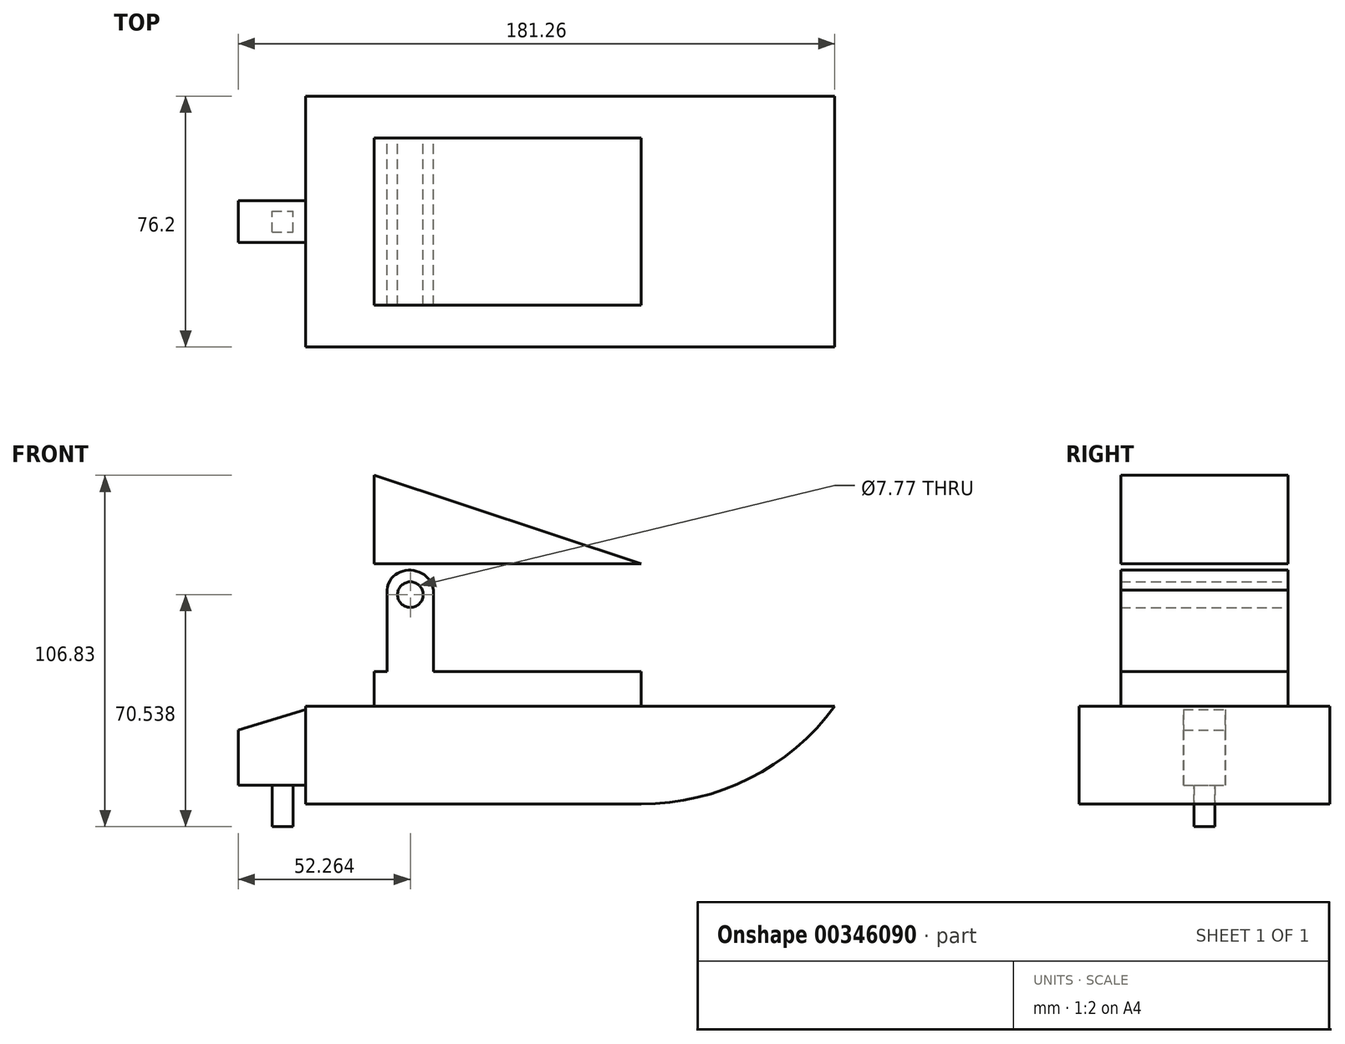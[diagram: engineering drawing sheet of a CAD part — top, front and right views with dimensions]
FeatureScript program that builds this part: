
annotation { "Feature Type Name" : "Feature", "Feature Type Description" : "" }
export const myFeature = defineFeature(function(context is Context, id is Id, definition is map)
    precondition{}
    {
        {
            var Q0;
            Q0=qCreatedBy(makeId("Front.planeOp"),FACE);
            var sketch = newSketch(context, id + "F0", { "sketchPlane" : qUnion([Q0])});
            skLineSegment(sketch, "E0", {"start": v(-51.12, -22.56) * mm, "end": v(50.84, -22.56) * mm});
            skArc(sketch, "E1", {"start": v(50.84, -22.56) * mm, "mid": v(83.8, -14.71) * mm, "end": v(109.67, 7.14) * mm});
            skLineSegment(sketch, "E2", {"start": v(-51.12, -22.56) * mm, "end": v(-51.12, 7.14) * mm});
            skLineSegment(sketch, "E3", {"start": v(-51.12, 7.14) * mm, "end": v(109.67, 7.14) * mm});
            skLineSegment(sketch, "E4", {"start": v(-30.27, 7.14) * mm, "end": v(-30.27, 17.7) * mm});
            skLineSegment(sketch, "E5", {"start": v(-30.27, 17.7) * mm, "end": v(-51.12, 17.7) * mm});
            skLineSegment(sketch, "E6", {"start": v(-51.12, 17.7) * mm, "end": v(-51.12, 7.14) * mm});
            skLineSegment(sketch, "E7", {"start": v(-30.27, 17.7) * mm, "end": v(109.67, 17.7) * mm});
            skLineSegment(sketch, "E8", {"start": v(109.67, 17.7) * mm, "end": v(109.67, 7.14) * mm});
            skLineSegment(sketch, "E9", {"start": v(-5.42, 17.7) * mm, "end": v(-5.42, 7.14) * mm});
            skLineSegment(sketch, "E10", {"start": v(-5.42, 7.14) * mm, "end": v(21.13, 7.14) * mm});
            skLineSegment(sketch, "E11", {"start": v(21.13, 7.14) * mm, "end": v(21.13, 17.7) * mm});
            skLineSegment(sketch, "E12", {"start": v(21.13, 17.7) * mm, "end": v(45.7, 17.7) * mm});
            skLineSegment(sketch, "E13", {"start": v(45.7, 17.7) * mm, "end": v(45.7, 7.14) * mm});
            skLineSegment(sketch, "E14", {"start": v(45.7, 7.14) * mm, "end": v(71.97, 7.14) * mm});
            skLineSegment(sketch, "E15", {"start": v(71.97, 7.14) * mm, "end": v(71.97, 17.7) * mm});
            skLineSegment(sketch, "E16", {"start": v(71.97, 17.7) * mm, "end": v(93.1, 17.7) * mm});
            skLineSegment(sketch, "E17", {"start": v(93.1, 17.7) * mm, "end": v(93.1, 7.14) * mm});
            skLineSegment(sketch, "E18.bottom", {"start": v(-30.27, 7.14) * mm, "end": v(50.84, 7.14) * mm});
            skLineSegment(sketch, "E18.left", {"start": v(-30.27, 7.14) * mm, "end": v(-30.27, 50.55) * mm});
            skLineSegment(sketch, "E18.right", {"start": v(50.84, 7.14) * mm, "end": v(50.84, 50.55) * mm});
            skLineSegment(sketch, "E19", {"start": v(-30.27, 50.55) * mm, "end": v(-30.27, 77.4) * mm});
            skLineSegment(sketch, "E20", {"start": v(-30.27, 77.4) * mm, "end": v(50.84, 50.55) * mm});
            skLineSegment(sketch, "E21", {"start": v(50.84, 50.55) * mm, "end": v(-30.27, 50.55) * mm});
            skCircle(sketch, "E22", {"center": v(-19.33, 41.1) * mm, "radius": 3.88 * mm});
            skLineSegment(sketch, "E23", {"start": v(-26.4, 7.14) * mm, "end": v(-26.4, 42.53) * mm});
            skFitSpline(sketch, "E24", {"points": [v(-26.4, 42.53) * mm, v(-12.33, 42.53) * mm], "startDerivative": vector(2.36, 24.06) * mm, "endDerivative": vector(3.84, -23.97) * mm});
            skLineSegment(sketch, "E25", {"start": v(-12.33, 42.53) * mm, "end": v(-12.33, 7.14) * mm});
            skCircle(sketch, "E26", {"center": v(0, 36.24) * mm, "radius": 8.65 * mm});
            skLineSegment(sketch, "E27", {"start": v(-51.12, 6.15) * mm, "end": v(-71.59, 0) * mm});
            skLineSegment(sketch, "E28", {"start": v(-71.59, 0) * mm, "end": v(-71.59, -16.87) * mm});
            skLineSegment(sketch, "E29", {"start": v(-71.59, -16.87) * mm, "end": v(-51.12, -16.87) * mm});
            skLineSegment(sketch, "E30", {"start": v(-61.35, -16.87) * mm, "end": v(-61.35, -29.44) * mm});
            skLineSegment(sketch, "E31", {"start": v(-61.35, -29.44) * mm, "end": v(-55.02, -29.44) * mm});
            skLineSegment(sketch, "E32", {"start": v(-55.02, -29.44) * mm, "end": v(-55.02, -16.87) * mm});
            skCircle(sketch, "E33", {"center": v(21.8, 36.24) * mm, "radius": 9.07 * mm});
            skLineSegment(sketch, "E34", {"start": v(44.16, 52.76) * mm, "end": v(44.16, 74.5) * mm});
            skLineSegment(sketch, "E35", {"start": v(16.55, 61.9) * mm, "end": v(16.55, 89.36) * mm});
            skSolve(sketch);
        }
        {
            var Q0;
            {var subQ15=sQuery(id+"F0.wireOp",EDGE,"E0");Q0=makeQuery(id+"F0.imprint","IMPRINT",FACE,{"disambiguationData":[TD([[makeQuery(id+"F0.imprint","IMPRINT",EDGE,{"derivedFrom":subQ15}),1.0]])]});}
            extrude(context, id + "F1", {"entities" : qUnion([Q0]), "endBound" : BoundingType.SYMMETRIC, "depth" : 76.2 * mm});
        }
        {
            var Q0;
            {var subQ3=sQuery(id+"F0.wireOp",EDGE,"E27");Q0=makeQuery(id+"F0.imprint","IMPRINT",FACE,{"disambiguationData":[TD([[makeQuery(id+"F0.imprint","IMPRINT",EDGE,{"derivedFrom":subQ3}),1.0]])]});}
            extrude(context, id + "F2", {"entities" : qUnion([Q0]), "operationType" : NewBodyOperationType.ADD, "endBound" : BoundingType.SYMMETRIC, "depth" : 12.7 * mm});
        }
        {
            var Q0;
            {var subQ0=sQuery(id+"F0.wireOp",EDGE,"E30");Q0=makeQuery(id+"F0.imprint","IMPRINT",FACE,{"disambiguationData":[TD([[makeQuery(id+"F0.imprint","IMPRINT",EDGE,{"derivedFrom":subQ0}),1.0]])]});}
            extrude(context, id + "F3", {"entities" : qUnion([Q0]), "operationType" : NewBodyOperationType.ADD, "endBound" : BoundingType.SYMMETRIC, "depth" : 6.35 * mm});
        }
        {
            var Q0;
            {var subQ7=sQuery(id+"F0.wireOp",EDGE,"E12");Q0=makeQuery(id+"F0.imprint","IMPRINT",FACE,{"disambiguationData":[TD([[makeQuery(id+"F0.imprint","IMPRINT",EDGE,{"derivedFrom":subQ7}),1.0]])]});}
            var Q1;
            {var subQ0=sQuery(id+"F0.wireOp",EDGE,"E13");Q1=makeQuery(id+"F0.imprint","IMPRINT",FACE,{"disambiguationData":[TD([[makeQuery(id+"F0.imprint","IMPRINT",EDGE,{"derivedFrom":subQ0}),1.0]])]});}
            var Q2;
            {var subQ0=sQuery(id+"F0.wireOp",EDGE,"E11");Q2=makeQuery(id+"F0.imprint","IMPRINT",FACE,{"disambiguationData":[TD([[makeQuery(id+"F0.imprint","IMPRINT",EDGE,{"derivedFrom":subQ0}),-1.0]])]});}
            var Q3;
            {var subQ0=sQuery(id+"F0.wireOp",EDGE,"E9");Q3=makeQuery(id+"F0.imprint","IMPRINT",FACE,{"disambiguationData":[TD([[makeQuery(id+"F0.imprint","IMPRINT",EDGE,{"derivedFrom":subQ0}),1.0]])]});}
            var Q4;
            {var subQ0=sQuery(id+"F0.wireOp",EDGE,"E9");Q4=makeQuery(id+"F0.imprint","IMPRINT",FACE,{"disambiguationData":[TD([[makeQuery(id+"F0.imprint","IMPRINT",EDGE,{"derivedFrom":subQ0}),-1.0]])]});}
            var Q5;
            {var subQ0=sQuery(id+"F0.wireOp",EDGE,"E23");var subQ1=sQuery(id+"F0.wireOp",EDGE,"E7");var subQ2=makeQuery(id+"F0.imprint","INTERSECT",VERTEX,{"derivedFrom":[subQ1,subQ0]});Q5=makeQuery(id+"F0.imprint","IMPRINT",FACE,{"disambiguationData":[TD([[makeQuery(id+"F0.imprint","IMPRINT",EDGE,{"disambiguationData":[TD([[subQ2,-1.0]])],"derivedFrom":subQ1}),-1.0]])]});}
            var Q6;
            {var subQ3=sQuery(id+"F0.wireOp",EDGE,"E23");var subQ5=sQuery(id+"F0.wireOp",EDGE,"E18.bottom");var subQ7=makeQuery(id+"F0.imprint","INTERSECT",VERTEX,{"derivedFrom":[subQ5,subQ3]});Q6=makeQuery(id+"F0.imprint","IMPRINT",FACE,{"disambiguationData":[TD([[makeQuery(id+"F0.imprint","IMPRINT",EDGE,{"disambiguationData":[TD([[subQ7,-1.0]])],"derivedFrom":subQ3}),1.0]])]});}
            var Q7;
            Q7=makeQuery(id+"F0.imprint","IMPRINT",FACE,{"disambiguationData":[TD([[makeQuery(id+"F0.imprint","IMPRINT",EDGE,{"derivedFrom":sQuery(id+"F0.wireOp",EDGE,"E22")}),-1.0]])]});
            var Q8;
            {var subQ4=sQuery(id+"F0.wireOp",EDGE,"E19");Q8=makeQuery(id+"F0.imprint","IMPRINT",FACE,{"disambiguationData":[TD([[makeQuery(id+"F0.imprint","IMPRINT",EDGE,{"derivedFrom":subQ4}),-1.0]])]});}
            extrude(context, id + "F4", {"entities" : qUnion([Q0, Q1, Q2, Q3, Q4, Q5, Q6, Q7, Q8]), "operationType" : NewBodyOperationType.ADD, "endBound" : BoundingType.SYMMETRIC, "depth" : 50.8 * mm});
        }
    });
